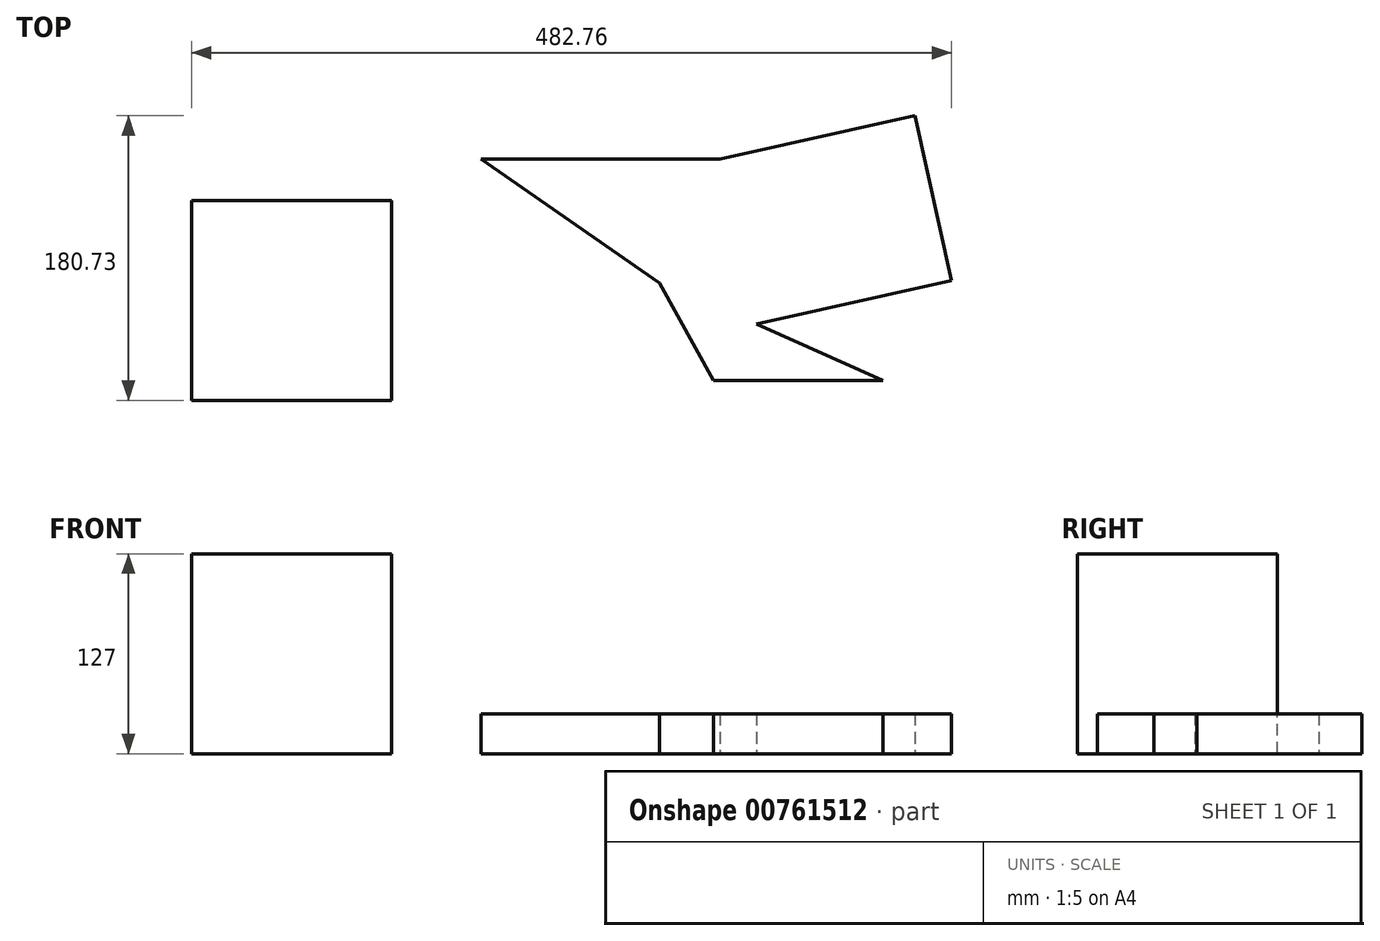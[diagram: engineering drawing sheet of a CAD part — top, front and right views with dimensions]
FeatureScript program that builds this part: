
annotation { "Feature Type Name" : "Feature", "Feature Type Description" : "" }
export const myFeature = defineFeature(function(context is Context, id is Id, definition is map)
    precondition{}
    {
        {
            var Q0;
            Q0=qCreatedBy(makeId("Front.planeOp"),FACE);
            var sketch = newSketch(context, id + "F0", { "sketchPlane" : qUnion([Q0])});
            skLineSegment(sketch, "E0.bottom", {"start": v(0, 0) * mm, "end": v(-127, 0) * mm});
            skLineSegment(sketch, "E0.top", {"start": v(0, 127) * mm, "end": v(-127, 127) * mm});
            skLineSegment(sketch, "E0.left", {"start": v(0, 0) * mm, "end": v(0, 127) * mm});
            skLineSegment(sketch, "E0.right", {"start": v(-127, 0) * mm, "end": v(-127, 127) * mm});
            skSolve(sketch);
        }
        {
            var Q0;
            Q0=makeQuery(id+"F0.imprint","IMPRINT",FACE,{"disambiguationData":[TD([[makeQuery(id+"F0.imprint","IMPRINT",EDGE,{"derivedFrom":sQuery(id+"F0.wireOp",EDGE,"E0.bottom")}),-1.0]])]});
            extrude(context, id + "F1", {"entities" : qUnion([Q0]), "depth" : 127 * mm, "offsetDistance" : 25.4 * mm});
        }
        {
            var Q0;
            Q0=qCreatedBy(makeId("Top.planeOp"),FACE);
            var sketch = newSketch(context, id + "F2", { "sketchPlane" : qUnion([Q0])});
            skLineSegment(sketch, "E1", {"start": v(57, 26.37) * mm, "end": v(208.64, 26.37) * mm});
            skLineSegment(sketch, "E2", {"start": v(208.64, 26.37) * mm, "end": v(231.74, -78.4) * mm});
            skLineSegment(sketch, "E3", {"start": v(231.74, -78.4) * mm, "end": v(312.34, -114.47) * mm});
            skLineSegment(sketch, "E4", {"start": v(312.34, -114.47) * mm, "end": v(204.47, -114.47) * mm});
            skLineSegment(sketch, "E5", {"start": v(204.47, -114.47) * mm, "end": v(170.17, -52.42) * mm});
            skLineSegment(sketch, "E6", {"start": v(170.17, -52.42) * mm, "end": v(57, 26.37) * mm});
            skSolve(sketch);
        }
        {
            var Q0;
            Q0 = qSketchRegion(id + "F2", true);
            extrude(context, id + "F3", {"entities" : qUnion([Q0]), "depth" : 25.4 * mm, "offsetDistance" : 25.4 * mm});
        }
        {
            var Q0;
            Q0=makeQuery(id+"F3.opExtrude","SWEPT_FACE",FACE,{"disambiguationData":[OSD([sQuery(id+"F2.wireOp",EDGE,"E2")])]});
            extrude(context, id + "F4", {"entities" : qUnion([Q0]), "operationType" : NewBodyOperationType.ADD, "depth" : 127 * mm, "offsetDistance" : 25.4 * mm});
        }
    });
